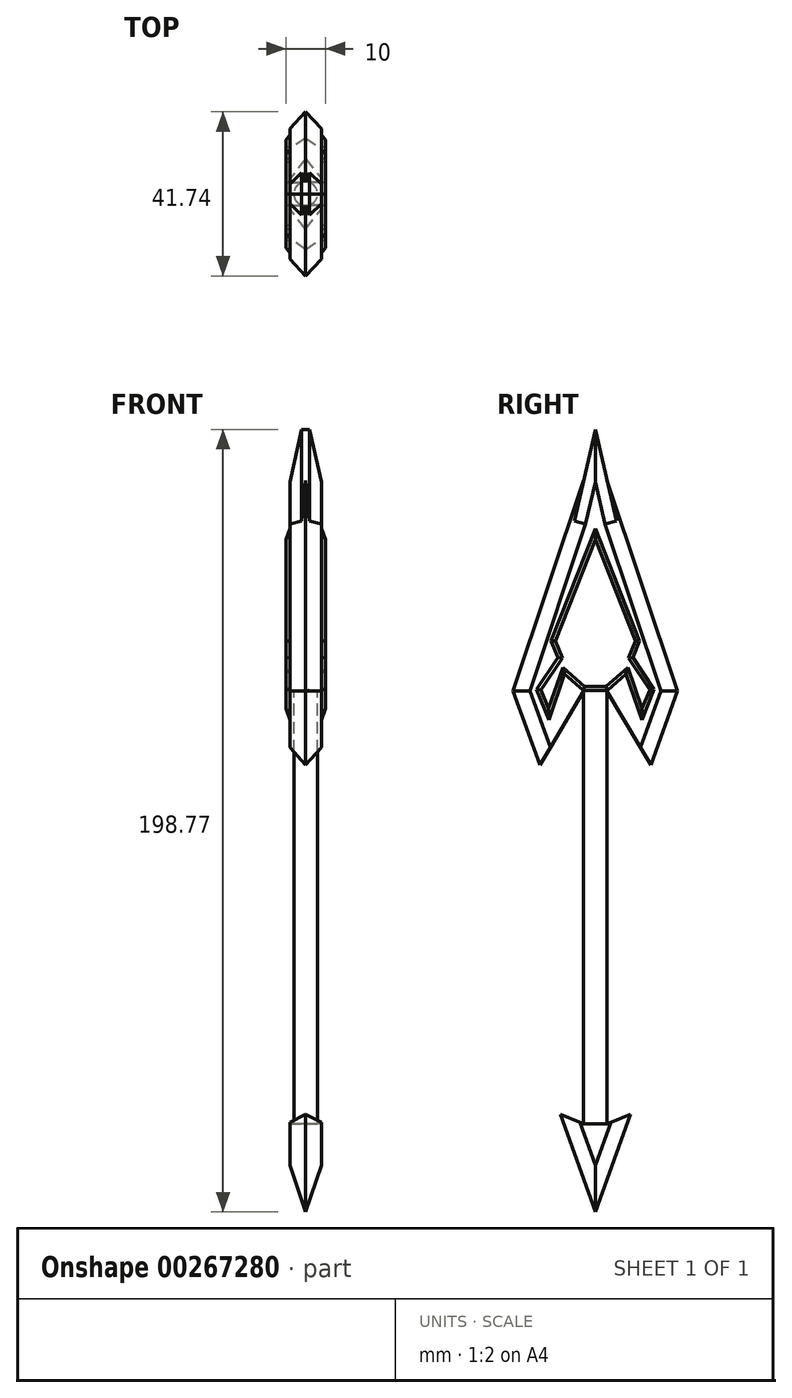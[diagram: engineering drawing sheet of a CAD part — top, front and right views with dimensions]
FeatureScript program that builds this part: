
annotation { "Feature Type Name" : "Feature", "Feature Type Description" : "" }
export const myFeature = defineFeature(function(context is Context, id is Id, definition is map)
    precondition{}
    {
        {
            var Q0;
            Q0=qCreatedBy(makeId("Right.planeOp"),FACE);
            var sketch = newSketch(context, id + "F0", { "sketchPlane" : qUnion([Q0])});
            skPoint(sketch, "E0.endSnap0", {"position": v(1.5, 0) * mm});
            skLineSegment(sketch, "E1", {"start": v(-3, 0) * mm, "end": v(-3, 55) * mm});
            skLineSegment(sketch, "E2", {"start": v(-3, 55) * mm, "end": v(3, 55) * mm});
            skLineSegment(sketch, "E3", {"start": v(3, 55) * mm, "end": v(3, 0) * mm});
            skLineSegment(sketch, "E4", {"start": v(3, 0) * mm, "end": v(3, -55) * mm});
            skLineSegment(sketch, "E5", {"start": v(3, -55) * mm, "end": v(-3, -55) * mm});
            skLineSegment(sketch, "E6", {"start": v(-3, -55) * mm, "end": v(-3, 0) * mm});
            skPoint(sketch, "E0.start.orphan", {"position": v(0, 0) * mm});
            skPoint(sketch, "E7.5.internal.snap0", {"position": v(3, 27.5) * mm});
            skPoint(sketch, "E7.6.internal.snap0", {"position": v(0, 55) * mm});
            skPoint(sketch, "E7.7.internal.snap0", {"position": v(0, 55) * mm});
            skPoint(sketch, "E7.3.internal.orphan", {"position": v(16.99, 55) * mm});
            skPoint(sketch, "E7.5.internal.orphan", {"position": v(3, 108.46) * mm});
            skPoint(sketch, "E7.6.internal.orphan", {"position": v(0, 121.46) * mm});
            skPoint(sketch, "E7.7.internal.orphan", {"position": v(0, 60.49) * mm});
            skLineSegment(sketch, "E8", {"start": v(3, 55) * mm, "end": v(14.1, 36.27) * mm});
            skLineSegment(sketch, "E9", {"start": v(14.1, 36.27) * mm, "end": v(20.87, 55) * mm});
            skLineSegment(sketch, "E10", {"start": v(20.87, 55) * mm, "end": v(3, 108.46) * mm});
            skLineSegment(sketch, "E11", {"start": v(3, 108.46) * mm, "end": v(0, 121.46) * mm});
            skLineSegment(sketch, "E12.MirrorCS", {"start": v(-3, 55) * mm, "end": v(-14.1, 36.27) * mm});
            skLineSegment(sketch, "E13.MirrorCS", {"start": v(-14.1, 36.27) * mm, "end": v(-20.87, 55) * mm});
            skLineSegment(sketch, "E14.MirrorCS", {"start": v(-20.87, 55) * mm, "end": v(-3, 108.46) * mm});
            skLineSegment(sketch, "E15.MirrorCS", {"start": v(-3, 108.46) * mm, "end": v(0, 121.46) * mm});
            skLineSegment(sketch, "E16", {"start": v(-3, -55) * mm, "end": v(-8.9, -52.6) * mm});
            skLineSegment(sketch, "E17", {"start": v(-8.9, -52.6) * mm, "end": v(0, -77.31) * mm});
            skLineSegment(sketch, "E18.MirrorCS", {"start": v(3, -55) * mm, "end": v(8.9, -52.6) * mm});
            skLineSegment(sketch, "E19.MirrorCS", {"start": v(8.9, -52.6) * mm, "end": v(0, -77.31) * mm});
            skSolve(sketch);
        }
        {
            var Q0;
            Q0=makeQuery(id+"F0.imprint","IMPRINT",FACE,{"disambiguationData":[TD([[makeQuery(id+"F0.imprint","IMPRINT",EDGE,{"derivedFrom":sQuery(id+"F0.wireOp",EDGE,"E1")}),-1.0]])]});
            extrude(context, id + "F1", {"entities" : qUnion([Q0]), "depth" : 3 * mm});
        }
        {
            var Q0;
            Q0=makeQuery(id+"F0.imprint","IMPRINT",FACE,{"disambiguationData":[TD([[makeQuery(id+"F0.imprint","IMPRINT",EDGE,{"derivedFrom":sQuery(id+"F0.wireOp",EDGE,"E1")}),-1.0]])]});
            extrude(context, id + "F2", {"entities" : qUnion([Q0]), "operationType" : NewBodyOperationType.ADD, "oppositeDirection" : true, "depth" : 3 * mm});
        }
        {
            var Q0;
            Q0=makeQuery(id+"F0.imprint","IMPRINT",FACE,{"disambiguationData":[TD([[makeQuery(id+"F0.imprint","IMPRINT",EDGE,{"derivedFrom":sQuery(id+"F0.wireOp",EDGE,"E2")}),1.0]])]});
            var sketch = newSketch(context, id + "F3", { "sketchPlane" : qUnion([Q0])});
            skLineSegment(sketch, "E20", {"start": v(-3.07, 55.2) * mm, "end": v(-7.8, 59.31) * mm});
            skLineSegment(sketch, "E21", {"start": v(-7.8, 59.31) * mm, "end": v(-11.23, 67.74) * mm});
            skLineSegment(sketch, "E22", {"start": v(-11.23, 67.74) * mm, "end": v(0, 96.28) * mm});
            skLineSegment(sketch, "E23", {"start": v(-9.52, 63.53) * mm, "end": v(-14.95, 55.44) * mm});
            skLineSegment(sketch, "E24", {"start": v(-14.95, 55.44) * mm, "end": v(-11.81, 47.72) * mm});
            skLineSegment(sketch, "E25", {"start": v(-11.81, 47.72) * mm, "end": v(-7.8, 59.31) * mm});
            skLineSegment(sketch, "E26.MirrorCS", {"start": v(11.23, 67.74) * mm, "end": v(0, 96.28) * mm});
            skLineSegment(sketch, "E27.MirrorCS", {"start": v(7.8, 59.31) * mm, "end": v(11.23, 67.74) * mm});
            skLineSegment(sketch, "E28.MirrorCS", {"start": v(9.52, 63.53) * mm, "end": v(14.95, 55.44) * mm});
            skLineSegment(sketch, "E29.MirrorCS", {"start": v(11.81, 47.72) * mm, "end": v(7.8, 59.31) * mm});
            skLineSegment(sketch, "E30.MirrorCS", {"start": v(3.07, 55.2) * mm, "end": v(7.8, 59.31) * mm});
            skLineSegment(sketch, "E31.MirrorCS", {"start": v(14.95, 55.44) * mm, "end": v(11.81, 47.72) * mm});
            skLineSegment(sketch, "E32", {"start": v(3.07, 55.2) * mm, "end": v(-3.07, 55.2) * mm});
            skSolve(sketch);
        }
        {
            var Q0;
            Q0=makeQuery(id+"F0.imprint","IMPRINT",FACE,{"disambiguationData":[TD([[makeQuery(id+"F0.imprint","IMPRINT",EDGE,{"derivedFrom":sQuery(id+"F0.wireOp",EDGE,"E2")}),1.0]])]});
            extrude(context, id + "F4", {"entities" : qUnion([Q0]), "operationType" : NewBodyOperationType.ADD, "depth" : 4 * mm});
        }
        {
            var Q0;
            {var subQ7=sQuery(id+"F3.wireOp",EDGE,"E20");Q0=makeQuery(id+"F3.imprint","IMPRINT",FACE,{"disambiguationData":[TD([[makeQuery(id+"F3.imprint","IMPRINT",EDGE,{"derivedFrom":subQ7}),-1.0]])]});}
            var Q1;
            {var subQ2=sQuery(id+"F3.wireOp",EDGE,"E28.MirrorCS");Q1=makeQuery(id+"F3.imprint","IMPRINT",FACE,{"disambiguationData":[TD([[makeQuery(id+"F3.imprint","IMPRINT",EDGE,{"derivedFrom":subQ2}),-1.0]])]});}
            var Q2;
            Q2=makeQuery(id+"F0.imprint","IMPRINT",FACE,{"disambiguationData":[TD([[makeQuery(id+"F0.imprint","IMPRINT",EDGE,{"derivedFrom":sQuery(id+"F0.wireOp",EDGE,"E2")}),1.0]])]});
            extrude(context, id + "F5", {"entities" : qUnion([Q0, Q1, Q2]), "operationType" : NewBodyOperationType.ADD, "oppositeDirection" : true, "depth" : 4 * mm});
        }
        {
            var Q0;
            Q0=makeQuery(id+"F4.opExtrude","CAP_EDGE",EDGE,{"disambiguationData":[OSD([sQuery(id+"F0.wireOp",EDGE,"E10")])],"isStart":false});
            var Q1;
            Q1=makeQuery(id+"F4.opExtrude","CAP_EDGE",EDGE,{"disambiguationData":[OSD([sQuery(id+"F0.wireOp",EDGE,"E14.MirrorCS")])],"isStart":false});
            var Q2;
            Q2=makeQuery(id+"F4.opExtrude","CAP_EDGE",EDGE,{"disambiguationData":[OSD([sQuery(id+"F0.wireOp",EDGE,"E13.MirrorCS")])],"isStart":false});
            var Q3;
            Q3=makeQuery(id+"F4.opExtrude","CAP_EDGE",EDGE,{"disambiguationData":[OSD([sQuery(id+"F0.wireOp",EDGE,"E9")])],"isStart":false});
            var Q4;
            Q4=makeQuery(id+"F5.opExtrude","CAP_EDGE",EDGE,{"disambiguationData":[OSD([sQuery(id+"F0.wireOp",EDGE,"E14.MirrorCS")])],"isStart":false});
            var Q5;
            Q5=makeQuery(id+"F5.opExtrude","CAP_EDGE",EDGE,{"disambiguationData":[OSD([sQuery(id+"F0.wireOp",EDGE,"E10")])],"isStart":false});
            var Q6;
            Q6=makeQuery(id+"F5.opExtrude","CAP_EDGE",EDGE,{"disambiguationData":[OSD([sQuery(id+"F0.wireOp",EDGE,"E9")])],"isStart":false});
            var Q7;
            Q7=makeQuery(id+"F5.opExtrude","CAP_EDGE",EDGE,{"disambiguationData":[OSD([sQuery(id+"F0.wireOp",EDGE,"E13.MirrorCS")])],"isStart":false});
            var Q8;
            Q8=makeQuery(id+"F5.opExtrude","CAP_EDGE",EDGE,{"disambiguationData":[OSD([sQuery(id+"F0.wireOp",EDGE,"E2")])],"isStart":false});
            var Q9;
            Q9=makeQuery(id+"F4.opExtrude","CAP_EDGE",EDGE,{"disambiguationData":[OSD([sQuery(id+"F0.wireOp",EDGE,"E2")])],"isStart":false});
            chamfer(context, id + "F6", {"entities" : qUnion([Q0, Q1, Q2, Q3, Q4, Q5, Q6, Q7, Q8, Q9]), "width" : 4 * mm, "tangentPropagation" : true});
        }
        {
            var Q0;
            Q0=makeQuery(id+"F4.opExtrude","CAP_EDGE",EDGE,{"disambiguationData":[OSD([sQuery(id+"F0.wireOp",EDGE,"E11")])],"isStart":false});
            var Q1;
            Q1=makeQuery(id+"F4.opExtrude","CAP_EDGE",EDGE,{"disambiguationData":[OSD([sQuery(id+"F0.wireOp",EDGE,"E15.MirrorCS")])],"isStart":false});
            var Q2;
            Q2=makeQuery(id+"F5.opExtrude","CAP_EDGE",EDGE,{"disambiguationData":[OSD([sQuery(id+"F0.wireOp",EDGE,"E15.MirrorCS")])],"isStart":false});
            var Q3;
            Q3=makeQuery(id+"F5.opExtrude","CAP_EDGE",EDGE,{"disambiguationData":[OSD([sQuery(id+"F0.wireOp",EDGE,"E11")])],"isStart":false});
            chamfer(context, id + "F7", {"entities" : qUnion([Q0, Q1, Q2, Q3]), "width" : 3 * mm, "tangentPropagation" : true});
        }
        {
            var Q0;
            Q0=makeQuery(id+"F2.opExtrude","CAP_EDGE",EDGE,{"disambiguationData":[OSD([sQuery(id+"F0.wireOp",EDGE,"E1"),sQuery(id+"F0.wireOp",EDGE,"E6")])],"isStart":false});
            var Q1;
            Q1=makeQuery(id+"F2.opExtrude","CAP_EDGE",EDGE,{"disambiguationData":[OSD([sQuery(id+"F0.wireOp",EDGE,"E3"),sQuery(id+"F0.wireOp",EDGE,"E4")])],"isStart":false});
            var Q2;
            Q2=makeQuery(id+"F1.opExtrude","CAP_EDGE",EDGE,{"disambiguationData":[OSD([sQuery(id+"F0.wireOp",EDGE,"E3"),sQuery(id+"F0.wireOp",EDGE,"E4")])],"isStart":false});
            var Q3;
            Q3=makeQuery(id+"F1.opExtrude","CAP_EDGE",EDGE,{"disambiguationData":[OSD([sQuery(id+"F0.wireOp",EDGE,"E1"),sQuery(id+"F0.wireOp",EDGE,"E6")])],"isStart":false});
            fillet(context, id + "F8", {"entities" : qUnion([Q0, Q1, Q2, Q3]), "radius" : 3 * mm, "tangentPropagation" : true, "allowEdgeOverflow" : false});
        }
        {
            var Q0;
            Q0 = qSketchRegion(id + "F3", true);
            extrude(context, id + "F9", {"entities" : qUnion([Q0]), "operationType" : NewBodyOperationType.ADD, "depth" : 5 * mm});
        }
        {
            var Q0;
            Q0 = qSketchRegion(id + "F3", true);
            extrude(context, id + "F10", {"entities" : qUnion([Q0]), "operationType" : NewBodyOperationType.ADD, "oppositeDirection" : true, "depth" : 5 * mm});
        }
        {
            var Q0;
            Q0=makeQuery(id+"F9.opExtrude","CAP_FACE",FACE,{"disambiguationData":[OSD([sQuery(id+"F3.wireOp",EDGE,"E20"),sQuery(id+"F3.wireOp",EDGE,"E21"),sQuery(id+"F3.wireOp",EDGE,"E22"),sQuery(id+"F3.wireOp",EDGE,"E23"),sQuery(id+"F3.wireOp",EDGE,"E24"),sQuery(id+"F3.wireOp",EDGE,"E25"),sQuery(id+"F3.wireOp",EDGE,"E26.MirrorCS"),sQuery(id+"F3.wireOp",EDGE,"E27.MirrorCS"),sQuery(id+"F3.wireOp",EDGE,"E28.MirrorCS"),sQuery(id+"F3.wireOp",EDGE,"E29.MirrorCS"),sQuery(id+"F3.wireOp",EDGE,"E30.MirrorCS"),sQuery(id+"F3.wireOp",EDGE,"E31.MirrorCS"),sQuery(id+"F3.wireOp",EDGE,"E32")])],"isStart":false});
            var Q1;
            Q1=makeQuery(id+"F10.opExtrude","CAP_EDGE",EDGE,{"disambiguationData":[OSD([sQuery(id+"F3.wireOp",EDGE,"E22")])],"isStart":false});
            var Q2;
            Q2=makeQuery(id+"F10.opExtrude","CAP_FACE",FACE,{"disambiguationData":[OSD([sQuery(id+"F3.wireOp",EDGE,"E20"),sQuery(id+"F3.wireOp",EDGE,"E21"),sQuery(id+"F3.wireOp",EDGE,"E22"),sQuery(id+"F3.wireOp",EDGE,"E23"),sQuery(id+"F3.wireOp",EDGE,"E24"),sQuery(id+"F3.wireOp",EDGE,"E25"),sQuery(id+"F3.wireOp",EDGE,"E26.MirrorCS"),sQuery(id+"F3.wireOp",EDGE,"E27.MirrorCS"),sQuery(id+"F3.wireOp",EDGE,"E28.MirrorCS"),sQuery(id+"F3.wireOp",EDGE,"E29.MirrorCS"),sQuery(id+"F3.wireOp",EDGE,"E30.MirrorCS"),sQuery(id+"F3.wireOp",EDGE,"E31.MirrorCS"),sQuery(id+"F3.wireOp",EDGE,"E32")])],"isStart":false});
            chamfer(context, id + "F11", {"entities" : qUnion([Q0, Q1, Q2]), "width" : 1 * mm, "tangentPropagation" : true});
        }
        {
            var Q0;
            Q0=makeQuery(id+"F0.imprint","IMPRINT",FACE,{"disambiguationData":[TD([[makeQuery(id+"F0.imprint","IMPRINT",EDGE,{"derivedFrom":sQuery(id+"F0.wireOp",EDGE,"E5")}),1.0]])]});
            extrude(context, id + "F12", {"entities" : qUnion([Q0]), "operationType" : NewBodyOperationType.ADD, "depth" : 4 * mm});
        }
        {
            var Q0;
            Q0=makeQuery(id+"F0.imprint","IMPRINT",FACE,{"disambiguationData":[TD([[makeQuery(id+"F0.imprint","IMPRINT",EDGE,{"derivedFrom":sQuery(id+"F0.wireOp",EDGE,"E5")}),1.0]])]});
            extrude(context, id + "F13", {"entities" : qUnion([Q0]), "operationType" : NewBodyOperationType.ADD, "oppositeDirection" : true, "depth" : 4 * mm});
        }
        {
            var Q0;
            Q0=makeQuery(id+"F13.opExtrude","CAP_EDGE",EDGE,{"disambiguationData":[OSD([sQuery(id+"F0.wireOp",EDGE,"E17")])],"isStart":false});
            var Q1;
            Q1=makeQuery(id+"F13.opExtrude","CAP_EDGE",EDGE,{"disambiguationData":[OSD([sQuery(id+"F0.wireOp",EDGE,"E19.MirrorCS")])],"isStart":false});
            var Q2;
            Q2=makeQuery(id+"F12.opExtrude","CAP_EDGE",EDGE,{"disambiguationData":[OSD([sQuery(id+"F0.wireOp",EDGE,"E17")])],"isStart":false});
            var Q3;
            Q3=makeQuery(id+"F12.opExtrude","CAP_EDGE",EDGE,{"disambiguationData":[OSD([sQuery(id+"F0.wireOp",EDGE,"E19.MirrorCS")])],"isStart":false});
            chamfer(context, id + "F14", {"entities" : qUnion([Q0, Q1, Q2, Q3]), "width" : 4 * mm, "tangentPropagation" : true});
        }
    });
